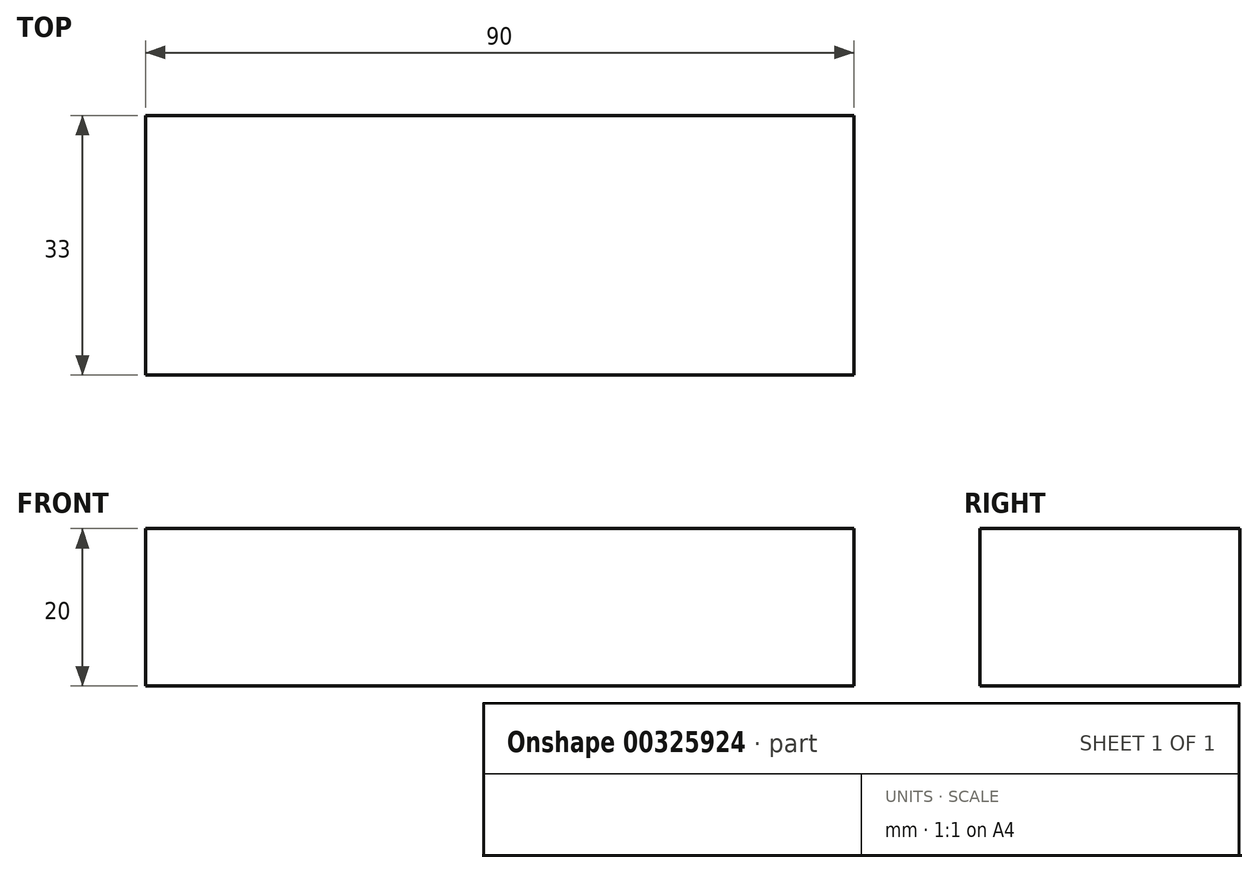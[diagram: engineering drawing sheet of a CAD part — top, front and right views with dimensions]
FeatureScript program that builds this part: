
annotation { "Feature Type Name" : "Feature", "Feature Type Description" : "" }
export const myFeature = defineFeature(function(context is Context, id is Id, definition is map)
    precondition{}
    {
        {
            var Q0;
            Q0=qCreatedBy(makeId("Top.planeOp"),FACE);
            var sketch = newSketch(context, id + "F0", { "sketchPlane" : qUnion([Q0])});
            skLineSegment(sketch, "E0.bottom", {"start": v(124.65, 130.14) * mm, "end": v(214.65, 130.14) * mm});
            skLineSegment(sketch, "E0.top", {"start": v(124.65, 97.14) * mm, "end": v(214.65, 97.14) * mm});
            skLineSegment(sketch, "E0.left", {"start": v(124.65, 130.14) * mm, "end": v(124.65, 97.14) * mm});
            skLineSegment(sketch, "E0.right", {"start": v(214.65, 130.14) * mm, "end": v(214.65, 97.14) * mm});
            skSolve(sketch);
        }
        {
            var Q0;
            Q0=makeQuery(id+"F0.imprint","IMPRINT",FACE,{"disambiguationData":[TD([[makeQuery(id+"F0.imprint","IMPRINT",EDGE,{"derivedFrom":sQuery(id+"F0.wireOp",EDGE,"E0.bottom")}),-1.0]])]});
            extrude(context, id + "F1", {"entities" : qUnion([Q0]), "depth" : 20 * mm});
        }
    });
